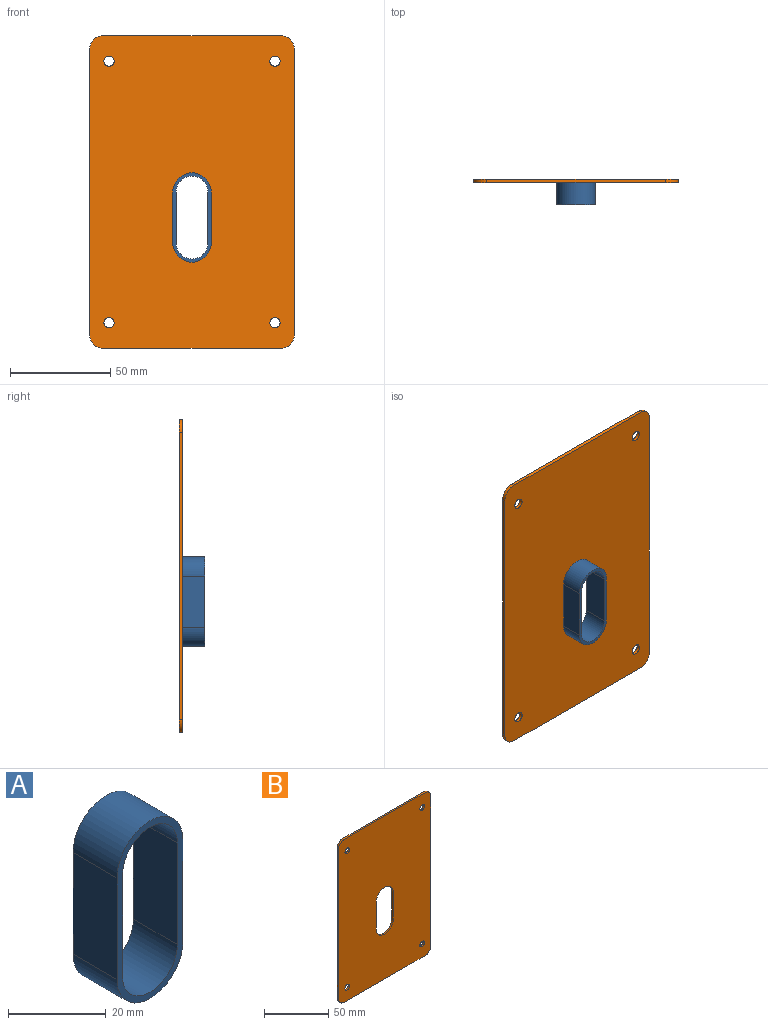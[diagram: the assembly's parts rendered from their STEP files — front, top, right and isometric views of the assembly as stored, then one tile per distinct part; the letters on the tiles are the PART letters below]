
ASSEMBLY  parts=2 mates=1
PART A: 10 faces, bbox 19.1x12.7x44.5 mm
  f0: plane 44.45x19.05mm, normal (0,-1,0), area 167.7mm2, adj f2,f3,f4,f5,f6,f7,f8,f9
  f1: plane 44.45x19.05mm, normal (0,1,0), area 167.7mm2, adj f2,f3,f4,f5,f6,f7,f8,f9
  f2: cylinder r=9.53mm len=19.05mm, axis (0,-1,0), area 380mm2, adj f0,f1,f3,f5
  f3: plane 25.4x12.7mm, normal (1,0,0), area 322.6mm2, adj f0,f1,f2,f4
  f4: cylinder r=9.53mm len=19.05mm, axis (0,-1,0), area 380mm2, adj f0,f1,f3,f5
  f5: plane 25.4x12.7mm, normal (-1,0,0), area 322.6mm2, adj f0,f1,f2,f4
  f6: cylinder r=7.94mm len=15.88mm, axis (0,-1,0), area 316.7mm2, adj f0,f1,f7,f9
  f7: plane 25.4x12.7mm, normal (-1,0,0), area 322.6mm2, adj f0,f1,f6,f8
  f8: cylinder r=7.94mm len=15.88mm, axis (0,-1,0), area 316.7mm2, adj f0,f1,f7,f9
  f9: plane 25.4x12.7mm, normal (1,0,0), area 322.6mm2, adj f0,f1,f6,f8
PART B: 18 faces, bbox 101.6x1.6x155.6 mm
  f0: plane 88.9x1.59mm, normal (0,0,-1), area 141.1mm2, adj f1,f15,f16,f17
  f1: cylinder r=6.35mm len=6.35mm, axis (0,-1,0), area 15.8mm2, adj f0,f2,f16,f17
  f2: plane 142.88x1.59mm, normal (-1,0,0), area 226.8mm2, adj f1,f3,f16,f17
  f3: cylinder r=6.35mm len=6.35mm, axis (0,-1,0), area 15.8mm2, adj f2,f4,f16,f17
  f4: plane 88.9x1.59mm, normal (0,0,1), area 141.1mm2, adj f3,f5,f16,f17
  f5: cylinder r=6.35mm len=6.35mm, axis (0,-1,0), area 15.8mm2, adj f4,f6,f16,f17
  f6: plane 142.88x1.59mm, normal (1,0,0), area 226.8mm2, adj f5,f15,f16,f17
  f7: plane 25.4x1.59mm, normal (-1,0,0), area 40.3mm2, adj f8,f14,f16,f17
  f8: cylinder r=9.53mm len=19.05mm, axis (0,-1,0), area 47.5mm2, adj f7,f9,f16,f17
  f9: plane 25.4x1.59mm, normal (1,0,0), area 40.3mm2, adj f8,f14,f16,f17
  f10: cylinder r=2.55mm len=5.11mm, axis (0,-1,0), area 25.5mm2, adj f16,f17
  f11: cylinder r=2.55mm len=5.11mm, axis (0,-1,0), area 25.5mm2, adj f16,f17
  f12: cylinder r=2.55mm len=5.11mm, axis (0,-1,0), area 25.5mm2, adj f16,f17
  f13: cylinder r=2.55mm len=5.11mm, axis (0,-1,0), area 25.5mm2, adj f16,f17
  f14: cylinder r=9.53mm len=19.05mm, axis (0,-1,0), area 47.5mm2, adj f7,f9,f16,f17
  f15: cylinder r=6.35mm len=6.35mm, axis (0,-1,0), area 15.8mm2, adj f0,f6,f16,f17
  f16: plane 155.58x101.6mm, normal (0,1,0), area 14921mm2, adj f0,f1,f2,f3,f4,f5,f6,f7
  f17: plane 155.58x101.6mm, normal (0,-1,0), area 14921mm2, adj f0,f1,f2,f3,f4,f5,f6,f7
PLACE A t=(-4.04,-22.64,-20.31)mm
PLACE B t=(-4.04,-22.64,5.09)mm
MATE fastened A.f4 <-> B.f8  axis (0,-1,0) through (-4.04,-22.64,5.09)mm
